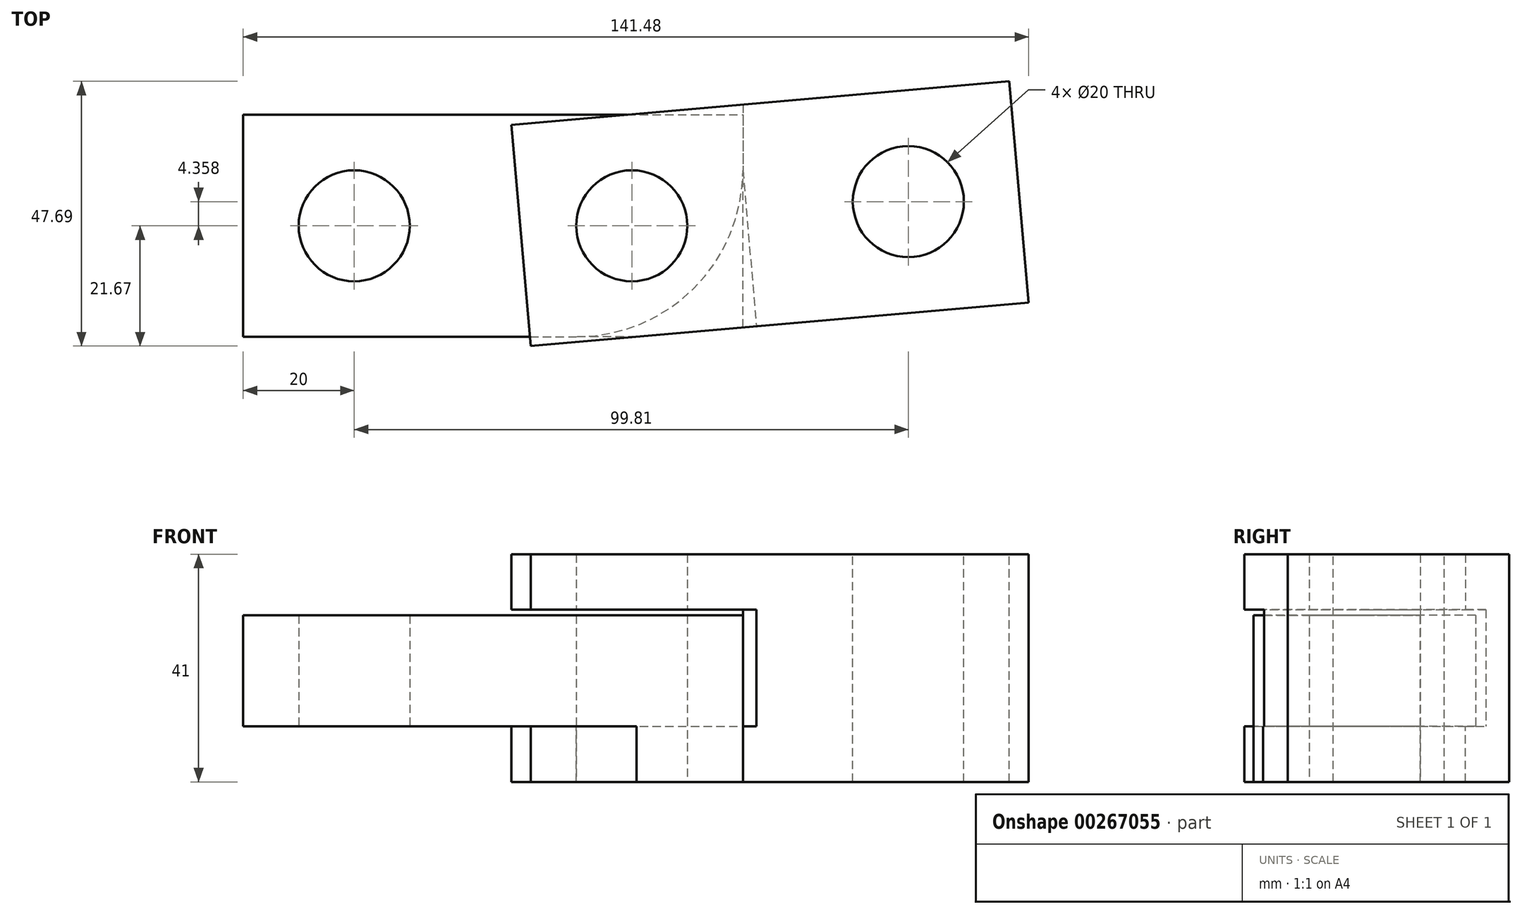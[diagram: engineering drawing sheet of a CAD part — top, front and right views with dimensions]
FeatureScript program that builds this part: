
annotation { "Feature Type Name" : "Feature", "Feature Type Description" : "" }
export const myFeature = defineFeature(function(context is Context, id is Id, definition is map)
    precondition{}
    {
        {
            var Q0;
            Q0=qCreatedBy(makeId("Top.planeOp"),FACE);
            var sketch = newSketch(context, id + "F0", { "sketchPlane" : qUnion([Q0])});
            skLineSegment(sketch, "E0", {"start": v(0, 0) * mm, "end": v(50, 0) * mm, "construction": true});
            skLineSegment(sketch, "E1.bottom", {"start": v(-20, 20) * mm, "end": v(70, 20) * mm});
            skLineSegment(sketch, "E1.top", {"start": v(-20, -20) * mm, "end": v(70, -20) * mm});
            skLineSegment(sketch, "E1.left", {"start": v(-20, 20) * mm, "end": v(-20, -20) * mm});
            skLineSegment(sketch, "E1.right", {"start": v(70, 20) * mm, "end": v(70, -20) * mm});
            skCircle(sketch, "E2", {"center": v(0, 0) * mm, "radius": 10 * mm});
            skCircle(sketch, "E3", {"center": v(50, 0) * mm, "radius": 10 * mm});
            skPoint(sketch, "E4", {"position": v(-20, 0) * mm});
            skLineSegment(sketch, "E5", {"start": v(50, 0) * mm, "end": v(99.8, 4.36) * mm, "construction": true});
            skSolve(sketch);
        }
        {
            var Q0;
            Q0=makeQuery(id+"F0.imprint","IMPRINT",FACE,{"disambiguationData":[TD([[makeQuery(id+"F0.imprint","IMPRINT",EDGE,{"derivedFrom":sQuery(id+"F0.wireOp",EDGE,"E1.bottom")}),-1.0]])]});
            extrude(context, id + "F1", {"entities" : qUnion([Q0]), "depth" : 20 * mm});
        }
        {
            var Q0;
            Q0=makeQuery(id+"F1.opExtrude","CAP_FACE",FACE,{"disambiguationData":[OSD([sQuery(id+"F0.wireOp",EDGE,"E1.bottom"),sQuery(id+"F0.wireOp",EDGE,"E1.top"),sQuery(id+"F0.wireOp",EDGE,"E1.left"),sQuery(id+"F0.wireOp",EDGE,"E1.right"),sQuery(id+"F0.wireOp",EDGE,"E2"),sQuery(id+"F0.wireOp",EDGE,"E3")])],"isStart":true});
            var sketch = newSketch(context, id + "F2", { "sketchPlane" : qUnion([Q0])});
            skLineSegment(sketch, "E6", {"start": v(50, 0) * mm, "end": v(99.8, -4.36) * mm, "construction": true});
            skLineSegment(sketch, "E7.bottom", {"start": v(31.82, 21.67) * mm, "end": v(121.48, 13.82) * mm});
            skLineSegment(sketch, "E7.top", {"start": v(28.33, -18.18) * mm, "end": v(118, -26.02) * mm});
            skLineSegment(sketch, "E7.left", {"start": v(31.82, 21.67) * mm, "end": v(28.33, -18.18) * mm});
            skLineSegment(sketch, "E7.right", {"start": v(121.48, 13.82) * mm, "end": v(118, -26.02) * mm});
            skLineSegment(sketch, "E8", {"start": v(50, 0) * mm, "end": v(0, 0) * mm, "construction": true});
            skPoint(sketch, "E9", {"position": v(30.08, 1.74) * mm});
            skCircle(sketch, "E10.0", {"center": v(50, 0) * mm, "radius": 10 * mm});
            skCircle(sketch, "E11", {"center": v(99.8, -4.36) * mm, "radius": 10 * mm});
            skSolve(sketch);
        }
        {
            var Q0;
            {var subQ0=sQuery(id+"F2.wireOp",EDGE,"E7.right");Q0=makeQuery(id+"F2.imprint","IMPRINT",FACE,{"disambiguationData":[TD([[makeQuery(id+"F2.imprint","IMPRINT",EDGE,{"derivedFrom":subQ0}),-1.0]])]});}
            var Q1;
            Q1=makeQuery(id+"F2.imprint","IMPRINT",FACE,{"disambiguationData":[TD([[makeQuery(id+"F2.imprint","IMPRINT",EDGE,{"derivedFrom":sQuery(id+"F2.wireOp",EDGE,"E10.0")}),1.0]])]});
            var Q2;
            {var subQ0=sQuery(id+"F2.wireOp",EDGE,"E7.left");var subQ1=sQuery(id+"F2.wireOp",EDGE,"E7.bottom");var subQ2=makeQuery(id+"F2.imprint","INTERSECT",VERTEX,{"derivedFrom":[subQ1,subQ0]});Q2=makeQuery(id+"F2.imprint","IMPRINT",FACE,{"disambiguationData":[TD([[makeQuery(id+"F2.imprint","IMPRINT",EDGE,{"disambiguationData":[TD([[subQ2,-1.0]])],"derivedFrom":subQ1}),-1.0]])]});}
            extrude(context, id + "F3", {"entities" : qUnion([Q0, Q1, Q2]), "depth" : 10 * mm});
        }
        {
            var Q0;
            Q0=makeQuery(id+"F1.opExtrude","CAP_FACE",FACE,{"disambiguationData":[OSD([sQuery(id+"F0.wireOp",EDGE,"E1.bottom"),sQuery(id+"F0.wireOp",EDGE,"E1.top"),sQuery(id+"F0.wireOp",EDGE,"E1.left"),sQuery(id+"F0.wireOp",EDGE,"E1.right"),sQuery(id+"F0.wireOp",EDGE,"E2"),sQuery(id+"F0.wireOp",EDGE,"E3")])],"isStart":false});
            var sketch = newSketch(context, id + "F4", { "sketchPlane" : qUnion([Q0])});
            skLineSegment(sketch, "E12.0", {"start": v(70, 20) * mm, "end": v(70, -20) * mm});
            skLineSegment(sketch, "E13.0", {"start": v(-20, 20) * mm, "end": v(70, 20) * mm});
            skLineSegment(sketch, "E14.0", {"start": v(-20, -20) * mm, "end": v(70, -20) * mm});
            skArc(sketch, "E15", {"start": v(40, -20) * mm, "mid": v(61.21, -11.21) * mm, "end": v(70, 10) * mm});
            skSolve(sketch);
        }
        {
            var Q0;
            {var subQ3=sQuery(id+"F4.wireOp",EDGE,"E15");Q0=makeQuery(id+"F4.imprint","IMPRINT",FACE,{"disambiguationData":[TD([[makeQuery(id+"F4.imprint","IMPRINT",EDGE,{"derivedFrom":subQ3}),-1.0]])]});}
            extrude(context, id + "F5", {"entities" : qUnion([Q0]), "operationType" : NewBodyOperationType.REMOVE, "endBound" : BoundingType.THROUGH_ALL, "oppositeDirection" : true, "depth" : 25 * mm});
        }
        {
            var Q0;
            Q0=makeQuery(id+"F3.opExtrude","CAP_FACE",FACE,{"disambiguationData":[OSD([sQuery(id+"F2.wireOp",EDGE,"E7.bottom"),sQuery(id+"F2.wireOp",EDGE,"E7.top"),sQuery(id+"F2.wireOp",EDGE,"E7.left"),sQuery(id+"F2.wireOp",EDGE,"E7.right"),sQuery(id+"F2.wireOp",EDGE,"E10.0"),sQuery(id+"F2.wireOp",EDGE,"E11")])],"isStart":true});
            var sketch = newSketch(context, id + "F6", { "sketchPlane" : qUnion([Q0])});
            skLineSegment(sketch, "E16.0", {"start": v(70, 20) * mm, "end": v(70, 10) * mm});
            skLineSegment(sketch, "E17", {"start": v(70, 10) * mm, "end": v(72.46, -18.11) * mm});
            skLineSegment(sketch, "E18", {"start": v(72.46, -18.11) * mm, "end": v(121.48, -13.82) * mm});
            skLineSegment(sketch, "E19", {"start": v(121.48, -13.82) * mm, "end": v(118, 26.02) * mm});
            skLineSegment(sketch, "E20", {"start": v(118, 26.02) * mm, "end": v(70, 21.83) * mm});
            skLineSegment(sketch, "E21", {"start": v(70, 21.83) * mm, "end": v(70, 20) * mm});
            skSolve(sketch);
        }
        {
            var Q0;
            Q0=makeQuery(id+"F6.imprint","IMPRINT",FACE,{"disambiguationData":[TD([[makeQuery(id+"F6.imprint","IMPRINT",EDGE,{"derivedFrom":sQuery(id+"F6.wireOp",EDGE,"E16.0")}),1.0]])]});
            extrude(context, id + "F7", {"entities" : qUnion([Q0]), "operationType" : NewBodyOperationType.ADD, "depth" : 21 * mm});
        }
        {
            var Q0;
            Q0=makeQuery(id+"F7.opExtrude","CAP_FACE",FACE,{"disambiguationData":[OSD([sQuery(id+"F2.wireOp",EDGE,"E11"),sQuery(id+"F6.wireOp",EDGE,"E16.0"),sQuery(id+"F6.wireOp",EDGE,"E17"),sQuery(id+"F6.wireOp",EDGE,"E18"),sQuery(id+"F6.wireOp",EDGE,"E19"),sQuery(id+"F6.wireOp",EDGE,"E20"),sQuery(id+"F6.wireOp",EDGE,"E21")])],"isStart":false});
            var sketch = newSketch(context, id + "F8", { "sketchPlane" : qUnion([Q0])});
            skLineSegment(sketch, "E22.0", {"start": v(31.82, -21.67) * mm, "end": v(72.46, -18.11) * mm});
            skLineSegment(sketch, "E23.0", {"start": v(72.46, -18.11) * mm, "end": v(121.48, -13.82) * mm});
            skLineSegment(sketch, "E24.0", {"start": v(121.48, -13.82) * mm, "end": v(118, 26.02) * mm});
            skLineSegment(sketch, "E25.0", {"start": v(70, 21.83) * mm, "end": v(118, 26.02) * mm});
            skLineSegment(sketch, "E26.0", {"start": v(28.33, 18.18) * mm, "end": v(70, 21.83) * mm});
            skLineSegment(sketch, "E27.0", {"start": v(31.82, -21.67) * mm, "end": v(28.33, 18.18) * mm});
            skCircle(sketch, "E28.0", {"center": v(99.8, 4.36) * mm, "radius": 10 * mm});
            skCircle(sketch, "E29.0", {"center": v(50, 0) * mm, "radius": 10 * mm});
            skSolve(sketch);
        }
        {
            var Q0;
            Q0=makeQuery(id+"F8.imprint","IMPRINT",FACE,{"disambiguationData":[TD([[makeQuery(id+"F8.imprint","IMPRINT",EDGE,{"derivedFrom":sQuery(id+"F8.wireOp",EDGE,"E23.0")}),1.0]])]});
            var Q1;
            Q1=makeQuery(id+"F8.imprint","IMPRINT",FACE,{"disambiguationData":[TD([[makeQuery(id+"F8.imprint","IMPRINT",EDGE,{"derivedFrom":sQuery(id+"F8.wireOp",EDGE,"E22.0")}),1.0]])]});
            extrude(context, id + "F9", {"entities" : qUnion([Q0, Q1]), "operationType" : NewBodyOperationType.ADD, "depth" : 10 * mm});
        }
    });
